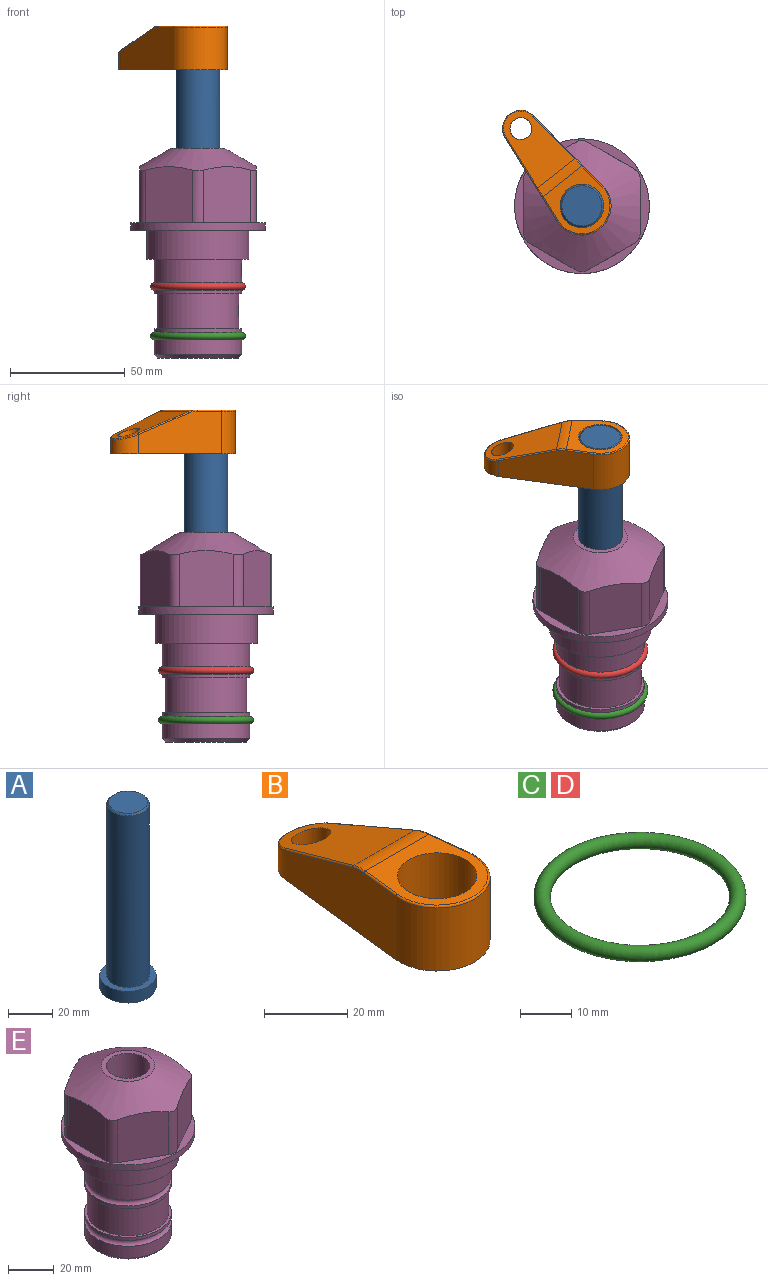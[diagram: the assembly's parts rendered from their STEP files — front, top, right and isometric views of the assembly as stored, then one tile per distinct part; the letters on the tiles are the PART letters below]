
ASSEMBLY  parts=5 mates=3
PART A: 6 faces, bbox 25.4x25.4x101.6 mm
  f0: plane 17.46x17.46mm, normal (0,0,1), area 239.5mm2, adj f5
  f1: plane 25.4x25.4mm, normal (0,0,-1), area 506.7mm2, adj f2
  f2: cylinder r=12.7mm len=25.4mm, axis (0,0,1), area 506.7mm2, adj f1,f3
  f3: plane 25.4x25.4mm, normal (0,0,1), area 221.7mm2, adj f2,f4
  f4: cylinder r=9.53mm len=94.46mm, axis (0,0,1), area 5653mm2, adj f3,f5
  f5: cone r=8.73mm half-angle=45deg, axis (0,0,-1), area 64.4mm2, adj f0,f4
PART B: 44 faces, bbox 27.5x64.5x19.1 mm
  f0: plane 2.3x0.95mm, normal (0,0,-1), area 1mm2, adj f25,f30,f34
  f1: plane 63.5x25.4mm, normal (0,0,-1), area 561.7mm2, adj f2,f3,f4,f5,f6,f7,f19,f20
  f2: cylinder r=12.7mm len=25.4mm, axis (0,0,-1), area 792.2mm2, adj f1,f3,f5,f13
  f3: plane 42.33x18.54mm, normal (0.99,0.11,0), area 647mm2, adj f1,f2,f4,f11,f12,f14
  f4: cylinder r=7.94mm len=15.78mm, axis (0,0,-1), area 158.6mm2, adj f1,f3,f5,f16
  f5: plane 42.33x18.54mm, normal (-0.99,0.11,0), area 647mm2, adj f1,f2,f4,f15,f17,f18
  f6: cylinder r=9.53mm len=19.05mm, axis (0,0,-1), area 1140.1mm2, adj f1,f8
  f7: cylinder r=4.76mm len=10.98mm, axis (0,0,-1), area 276.1mm2, adj f1,f9
  f8: plane 25.83x24.38mm, normal (0,0,1), area 262.2mm2, adj f6,f10,f11,f13,f15
  f9: plane 32.49x20.55mm, normal (0,0.34,0.94), area 489.9mm2, adj f7,f10,f14,f16,f18
  f10: cylinder r=12.7mm len=21.49mm, axis (-1,0,0), area 93.2mm2, adj f8,f9,f12,f17
  f11: cylinder r=0.51mm len=12.34mm, axis (0.11,-0.99,0), area 9.9mm2, adj f3,f8,f12,f13
  f12: bspline ~7.62x1.64mm, area 3.5mm2, adj f3,f10,f11,f14
  f13: torus R=12.19mm, axis (0,0,1), area 33.6mm2, adj f2,f8,f11,f15
  f14: cylinder r=0.51mm len=26.01mm, axis (0.1,-0.93,0.34), area 21.6mm2, adj f3,f9,f12,f16
  f15: cylinder r=0.51mm len=12.34mm, axis (0.11,0.99,0), area 9.9mm2, adj f5,f8,f13,f17
  f16: bspline ~15.78x7.05mm, area 15.7mm2, adj f4,f9,f14,f18
  f17: bspline ~7.62x1.64mm, area 3.5mm2, adj f5,f10,f15,f18
  f18: cylinder r=0.51mm len=26.01mm, axis (0.1,0.93,-0.34), area 21.6mm2, adj f5,f9,f16,f17
  f19: plane 21.6x14.29mm, normal (-0.99,-0.11,0), area 242.6mm2, adj f1,f26,f28,f34,f36,f38
  f20: plane 21.6x14.29mm, normal (0.99,-0.11,0), area 242.6mm2, adj f1,f27,f29,f37,f39,f41
  f21: cylinder r=12.7mm len=14.29mm, axis (0,0,-1), area 173.2mm2, adj f1,f26,f27,f30,f31,f33
  f22: cylinder r=7.94mm len=7.63mm, axis (0,0,-1), area 53.8mm2, adj f1,f28,f29,f42
  f23: plane 2.3x0.95mm, normal (0,0,-1), area 1mm2, adj f25,f33,f37
  f24: plane 17.94x12.32mm, normal (0,-0.34,-0.94), area 191.2mm2, adj f25,f38,f41,f42
  f25: cylinder r=9.53mm len=12.93mm, axis (-1,0,0), area 37.5mm2, adj f0,f23,f24,f31,f36,f39
  f26: cylinder r=1.59mm len=14.29mm, axis (0,0,-1), area 49mm2, adj f1,f19,f21,f32
  f27: cylinder r=1.59mm len=14.29mm, axis (0,0,-1), area 49mm2, adj f1,f20,f21,f35
  f28: cylinder r=1.59mm len=7.28mm, axis (0,0,-1), area 22.1mm2, adj f1,f19,f22,f40
  f29: cylinder r=1.59mm len=7.28mm, axis (0,0,-1), area 22.1mm2, adj f1,f20,f22,f43
  f30: torus R=14.29mm, axis (0,0,1), area 5.8mm2, adj f0,f21,f31,f32
  f31: bspline ~11.06x2.73mm, area 20.8mm2, adj f21,f25,f30,f33
  f32: sphere r=1.59mm, area 5.4mm2, adj f26,f30,f34
  f33: torus R=14.29mm, axis (0,0,1), area 5.8mm2, adj f21,f23,f31,f35
  f34: cylinder r=1.59mm len=1.68mm, axis (-0.11,0.99,0), area 2.4mm2, adj f0,f19,f32,f36
  f35: sphere r=1.59mm, area 5.4mm2, adj f27,f33,f37
  f36: bspline ~5.82x2.33mm, area 7.7mm2, adj f19,f25,f34,f38
  f37: cylinder r=1.59mm len=1.68mm, axis (0.11,0.99,0), area 2.4mm2, adj f20,f23,f35,f39
  f38: cylinder r=1.59mm len=18.33mm, axis (0.1,-0.93,0.34), area 46.7mm2, adj f19,f24,f36,f40
  f39: bspline ~5.82x2.33mm, area 7.7mm2, adj f20,f25,f37,f41
  f40: sphere r=1.59mm, area 3.6mm2, adj f28,f38,f42
  f41: cylinder r=1.59mm len=18.33mm, axis (0.1,0.93,-0.34), area 46.7mm2, adj f20,f24,f39,f43
  f42: bspline ~8.31x1.84mm, area 15.3mm2, adj f22,f24,f40,f43
  f43: sphere r=1.59mm, area 3.6mm2, adj f29,f41,f42
PART C: 1 faces, bbox 44.7x44.7x3.2 mm
  f0: torus R=19.05mm, axis (0,0,1), area 1193.9mm2
PART D: same geometry as C
PART E: 36 faces, bbox 58.7x58.7x91.2 mm
  f0: cylinder r=17.78mm len=35.56mm, axis (0,0,1), area 1670.8mm2, adj f23,f24,f31
  f1: cylinder r=19.05mm len=38.1mm, axis (0,0,1), area 1191.9mm2, adj f26,f27,f30
  f2: plane 58.66x58.66mm, normal (0,0,-1), area 1150.6mm2, adj f3,f28
  f3: cylinder r=29.33mm len=58.66mm, axis (0,0,-1), area 585.1mm2, adj f2,f4
  f4: plane 58.66x58.66mm, normal (0,0,1), area 475.9mm2, adj f3,f5,f6,f7,f8,f9,f10,f11
  f5: plane 24.5x20.32mm, normal (-0.5,0.87,0), area 562.8mm2, adj f4,f15,f16,f17
  f6: plane 24.5x20.32mm, normal (0.5,0.87,0), area 562.8mm2, adj f4,f14,f15,f17
  f7: plane 24.5x23.48mm, normal (1,0,0), area 562.8mm2, adj f4,f13,f14,f17
  f8: plane 24.5x20.32mm, normal (0.5,-0.87,0), area 562.8mm2, adj f4,f12,f13,f17
  f9: plane 24.5x20.32mm, normal (-0.5,-0.87,0), area 562.8mm2, adj f4,f11,f12,f17
  f10: plane 24.5x23.48mm, normal (-1,0,0), area 562.8mm2, adj f4,f11,f16,f17
  f11: cylinder r=5.08mm len=23.01mm, axis (0,0,-1), area 121.2mm2, adj f4,f9,f10,f17
  f12: cylinder r=5.08mm len=23.01mm, axis (0,0,-1), area 121.2mm2, adj f4,f8,f9,f17
  f13: cylinder r=5.08mm len=23.01mm, axis (0,0,-1), area 121.2mm2, adj f4,f7,f8,f17
  f14: cylinder r=5.08mm len=23.01mm, axis (0,0,-1), area 121.2mm2, adj f4,f6,f7,f17
  f15: cylinder r=5.08mm len=23.01mm, axis (0,0,-1), area 121.2mm2, adj f4,f5,f6,f17
  f16: cylinder r=5.08mm len=23.01mm, axis (0,0,-1), area 121.2mm2, adj f4,f5,f10,f17
  f17: cone r=11.73mm half-angle=60deg, axis (0,0,-1), area 2071.8mm2, adj f5,f6,f7,f8,f9,f10,f11,f12
  f18: plane 23.46x23.46mm, normal (0,0,1), area 147.4mm2, adj f17,f35
  f19: plane 34.93x34.93mm, normal (0,0,-1), area 958mm2, adj f29
  f20: cylinder r=19.05mm len=38.1mm, axis (0,0,1), area 760.1mm2, adj f21,f29
  f21: torus R=19.05mm, axis (0,0,1), area 565.3mm2, adj f20,f22
  f22: cylinder r=19.05mm len=38.1mm, axis (0,0,1), area 190mm2, adj f21,f23
  f23: plane 38.1x38.1mm, normal (0,0,1), area 146.9mm2, adj f0,f22
  f24: plane 38.1x38.1mm, normal (0,0,-1), area 146.9mm2, adj f0,f25
  f25: cylinder r=19.05mm len=38.1mm, axis (0,0,1), area 190mm2, adj f24,f26
  f26: torus R=19.05mm, axis (0,0,1), area 565.3mm2, adj f1,f25
  f27: plane 44.45x44.45mm, normal (0,0,-1), area 411.7mm2, adj f1,f28
  f28: cylinder r=22.23mm len=44.45mm, axis (0,0,1), area 1773.5mm2, adj f2,f27
  f29: cone r=19.05mm half-angle=45deg, axis (0,0,1), area 257.5mm2, adj f19,f20
  f30: cylinder r=3.17mm len=6.75mm, axis (-1,0,0), area 128mm2, adj f1,f33
  f31: cylinder r=3.17mm len=6.35mm, axis (-1,0,0), area 102.5mm2, adj f0,f33
  f32: plane 25.4x25.4mm, normal (0,0,1), area 506.7mm2, adj f33
  f33: cylinder r=12.7mm len=66.42mm, axis (0,0,-1), area 5236.2mm2, adj f30,f31,f32,f34
  f34: cone r=9.53mm half-angle=30deg, axis (0,0,-1), area 443.4mm2, adj f33,f35
  f35: cylinder r=9.53mm len=19.05mm, axis (0,0,-1), area 849mm2, adj f18,f34
PLACE A rot(axis=(0,0,1),128.3deg) t=(0,0,15.2)mm
PLACE B rot(axis=(0,0,1),38.3deg) t=(0,0,69.81)mm
PLACE C t=(0,0,-21.59)mm
PLACE D at identity
PLACE E at identity fixed
MATE fastened C.f0 <-> E.f0  axis (0,0,1) through (0,0,-46.1)mm
MATE cylindrical A.f2 <-> E.f0  axis (0,0,1) through (0,0,40.83)mm
MATE fastened B.f2 <-> A.f2  axis (0,0,1) through (0,0,88.86)mm
